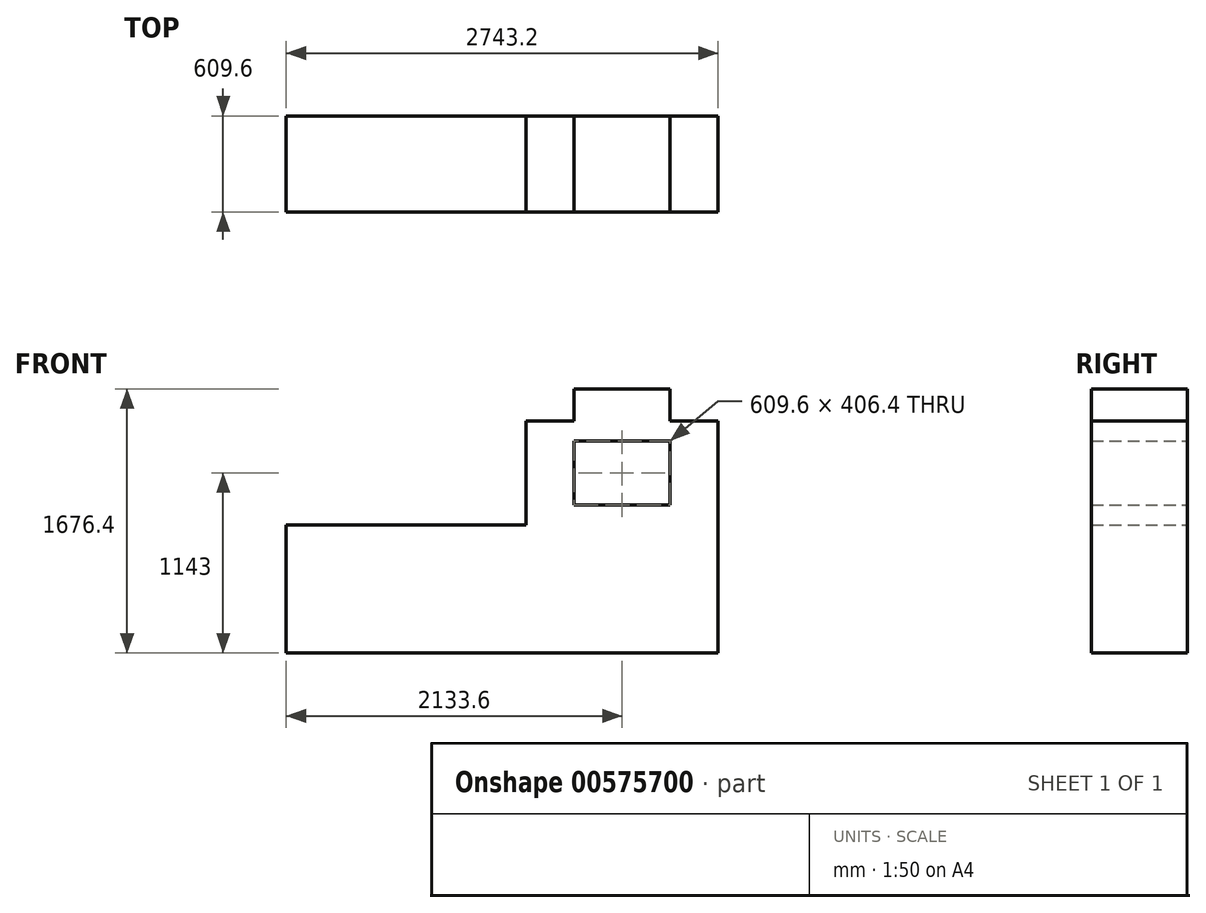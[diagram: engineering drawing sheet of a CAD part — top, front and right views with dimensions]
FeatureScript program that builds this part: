
annotation { "Feature Type Name" : "Feature", "Feature Type Description" : "" }
export const myFeature = defineFeature(function(context is Context, id is Id, definition is map)
    precondition{}
    {
        {
            var Q0;
            Q0=qCreatedBy(makeId("Front.planeOp"),FACE);
            var sketch = newSketch(context, id + "F0", { "sketchPlane" : qUnion([Q0])});
            skLineSegment(sketch, "E0", {"start": v(0, 0) * mm, "end": v(2743.2, 0) * mm});
            skLineSegment(sketch, "E1", {"start": v(2743.2, 0) * mm, "end": v(2743.2, 1473.2) * mm});
            skLineSegment(sketch, "E2", {"start": v(2743.2, 1473.2) * mm, "end": v(2438.4, 1473.2) * mm});
            skLineSegment(sketch, "E3", {"start": v(2438.4, 1473.2) * mm, "end": v(2438.4, 1676.4) * mm});
            skLineSegment(sketch, "E4", {"start": v(2438.4, 1676.4) * mm, "end": v(1828.8, 1676.4) * mm});
            skLineSegment(sketch, "E5", {"start": v(1828.8, 1676.4) * mm, "end": v(1828.8, 1473.2) * mm});
            skLineSegment(sketch, "E6", {"start": v(1828.8, 1473.2) * mm, "end": v(1524, 1473.2) * mm});
            skLineSegment(sketch, "E7", {"start": v(0, 0) * mm, "end": v(0, 812.8) * mm});
            skLineSegment(sketch, "E8", {"start": v(0, 812.8) * mm, "end": v(1524, 812.8) * mm});
            skLineSegment(sketch, "E9", {"start": v(1524, 812.8) * mm, "end": v(1524, 1473.2) * mm});
            skLineSegment(sketch, "E10", {"start": v(1828.8, 1346.2) * mm, "end": v(1828.8, 939.8) * mm});
            skLineSegment(sketch, "E11", {"start": v(1828.8, 939.8) * mm, "end": v(2438.4, 939.8) * mm});
            skLineSegment(sketch, "E12", {"start": v(2438.4, 939.8) * mm, "end": v(2438.4, 1346.2) * mm});
            skLineSegment(sketch, "E13", {"start": v(1828.8, 1346.2) * mm, "end": v(2438.4, 1346.2) * mm});
            skSolve(sketch);
        }
        {
            var Q0;
            Q0=makeQuery(id+"F0.imprint","IMPRINT",FACE,{"disambiguationData":[TD([[makeQuery(id+"F0.imprint","IMPRINT",EDGE,{"derivedFrom":sQuery(id+"F0.wireOp",EDGE,"E0")}),1.0]])]});
            extrude(context, id + "F1", {"entities" : qUnion([Q0]), "depth" : 609.6 * mm, "offsetDistance" : 25.4 * mm});
        }
    });
